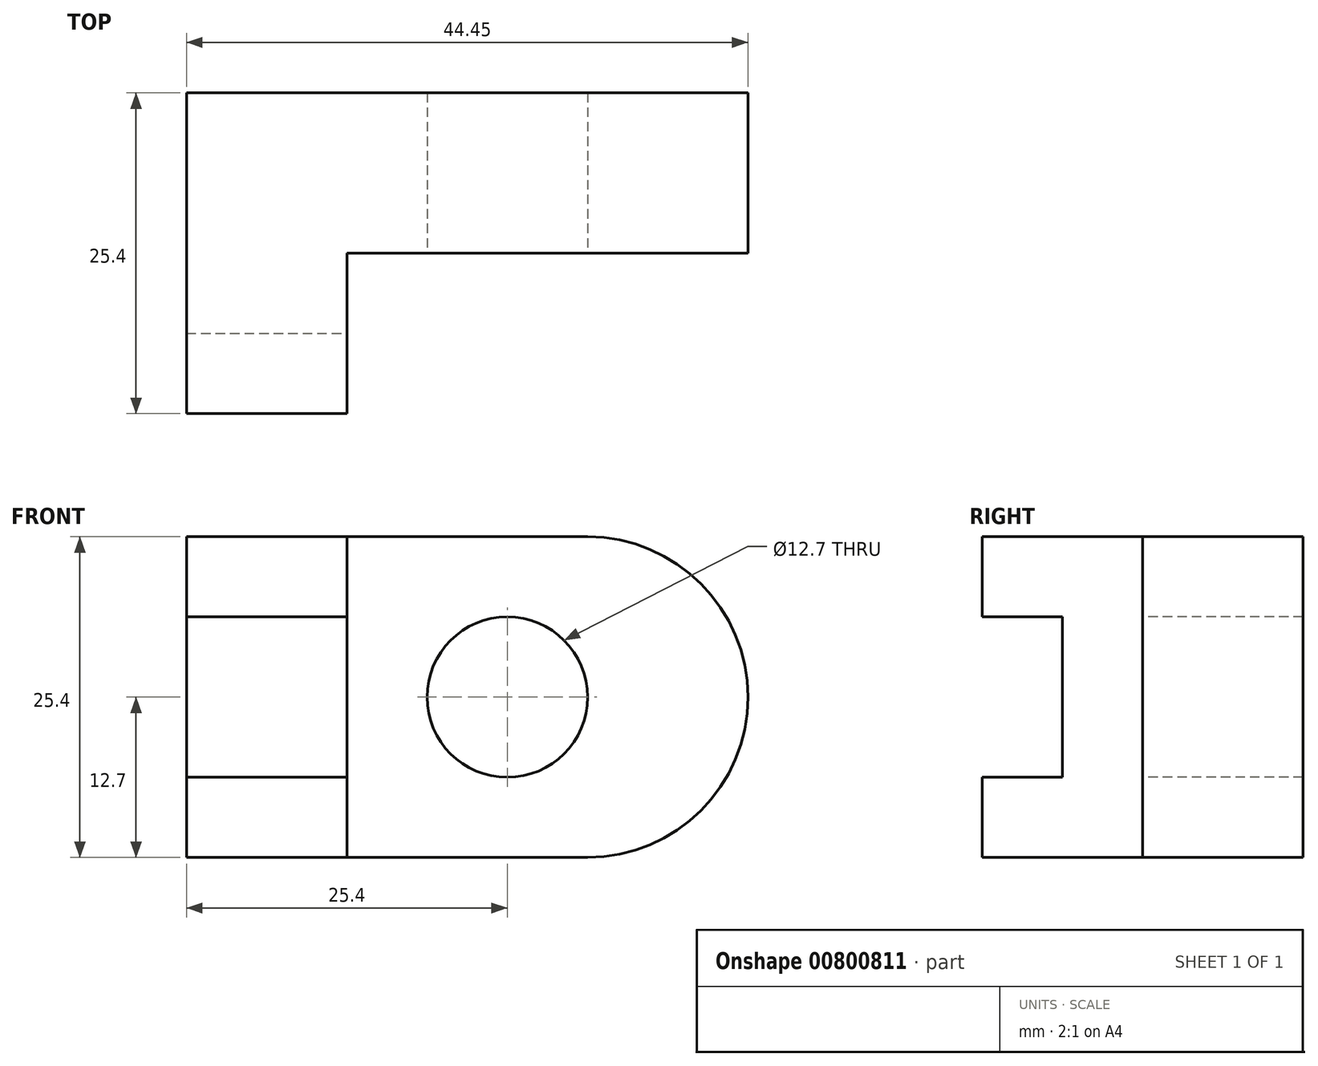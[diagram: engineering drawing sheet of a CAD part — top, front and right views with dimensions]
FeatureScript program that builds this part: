
annotation { "Feature Type Name" : "Feature", "Feature Type Description" : "" }
export const myFeature = defineFeature(function(context is Context, id is Id, definition is map)
    precondition{}
    {
        {
            var Q0;
            Q0=qCreatedBy(makeId("Top.planeOp"),FACE);
            var sketch = newSketch(context, id + "F0", { "sketchPlane" : qUnion([Q0])});
            skLineSegment(sketch, "E0", {"start": v(0, 0) * mm, "end": v(0, -12.7) * mm});
            skLineSegment(sketch, "E1", {"start": v(0, -12.7) * mm, "end": v(-12.7, -12.7) * mm});
            skLineSegment(sketch, "E2", {"start": v(-12.7, -12.7) * mm, "end": v(-12.7, 12.7) * mm});
            skLineSegment(sketch, "E3", {"start": v(-12.7, 12.7) * mm, "end": v(31.75, 12.7) * mm});
            skLineSegment(sketch, "E4", {"start": v(31.75, 12.7) * mm, "end": v(31.75, 0) * mm});
            skLineSegment(sketch, "E5", {"start": v(31.75, 0) * mm, "end": v(0, 0) * mm});
            skSolve(sketch);
        }
        {
            var Q0;
            Q0=makeQuery(id+"F0.imprint","IMPRINT",FACE,{"disambiguationData":[TD([[makeQuery(id+"F0.imprint","IMPRINT",EDGE,{"derivedFrom":sQuery(id+"F0.wireOp",EDGE,"E0")}),-1.0]])]});
            extrude(context, id + "F1", {"entities" : qUnion([Q0]), "depth" : 25.4 * mm, "offsetDistance" : 25.4 * mm});
        }
        {
            var Q0;
            Q0=makeQuery(id+"F1.opExtrude","SWEPT_FACE",FACE,{"disambiguationData":[OSD([sQuery(id+"F0.wireOp",EDGE,"E1")])]});
            var sketch = newSketch(context, id + "F2", { "sketchPlane" : qUnion([Q0])});
            skLineSegment(sketch, "E6", {"start": v(-12.7, 0) * mm, "end": v(-12.7, 6.35) * mm});
            skLineSegment(sketch, "E7", {"start": v(-12.7, 6.35) * mm, "end": v(0, 6.35) * mm});
            skLineSegment(sketch, "E8", {"start": v(0, 6.35) * mm, "end": v(0, 19.05) * mm});
            skLineSegment(sketch, "E9", {"start": v(0, 19.05) * mm, "end": v(-12.7, 19.05) * mm});
            skLineSegment(sketch, "E10", {"start": v(-12.7, 19.05) * mm, "end": v(-12.7, 6.35) * mm});
            skSolve(sketch);
        }
        {
            var Q0;
            Q0=makeQuery(id+"F2.imprint","IMPRINT",FACE,{"disambiguationData":[TD([[makeQuery(id+"F2.imprint","IMPRINT",EDGE,{"derivedFrom":sQuery(id+"F2.wireOp",EDGE,"E7")}),1.0]])]});
            extrude(context, id + "F3", {"entities" : qUnion([Q0]), "operationType" : NewBodyOperationType.REMOVE, "oppositeDirection" : true, "depth" : 6.35 * mm, "offsetDistance" : 25.4 * mm});
        }
        {
            var Q0;
            Q0=makeQuery(id+"F1.opExtrude","SWEPT_FACE",FACE,{"disambiguationData":[OSD([sQuery(id+"F0.wireOp",EDGE,"E5")])]});
            var sketch = newSketch(context, id + "F4", { "sketchPlane" : qUnion([Q0])});
            skLineSegment(sketch, "E11", {"start": v(0, 25.4) * mm, "end": v(12.7, 25.4) * mm, "construction": true});
            skLineSegment(sketch, "E12", {"start": v(0, 0) * mm, "end": v(12.7, 0) * mm, "construction": true});
            skLineSegment(sketch, "E13", {"start": v(12.7, 0) * mm, "end": v(19.05, 0) * mm, "construction": true});
            skLineSegment(sketch, "E14", {"start": v(12.7, 25.4) * mm, "end": v(19.05, 25.4) * mm, "construction": true});
            skArc(sketch, "E15", {"start": v(19.05, 0) * mm, "mid": v(31.75, 12.7) * mm, "end": v(19.05, 25.4) * mm});
            skLineSegment(sketch, "E16", {"start": v(19.05, 25.4) * mm, "end": v(0, 25.4) * mm});
            skLineSegment(sketch, "E17", {"start": v(19.05, 25.4) * mm, "end": v(31.75, 25.4) * mm});
            skLineSegment(sketch, "E18", {"start": v(31.75, 25.4) * mm, "end": v(31.75, 12.7) * mm});
            skLineSegment(sketch, "E19", {"start": v(19.05, 0) * mm, "end": v(31.75, 0) * mm});
            skLineSegment(sketch, "E20", {"start": v(31.75, 0) * mm, "end": v(31.75, 12.7) * mm});
            skSolve(sketch);
        }
        {
            var Q0;
            {var subQ0=sQuery(id+"F4.wireOp",EDGE,"E17");Q0=makeQuery(id+"F4.imprint","IMPRINT",FACE,{"disambiguationData":[TD([[makeQuery(id+"F4.imprint","IMPRINT",EDGE,{"derivedFrom":subQ0}),1.0]])]});}
            var Q1;
            {var subQ0=sQuery(id+"F4.wireOp",EDGE,"E19");Q1=makeQuery(id+"F4.imprint","IMPRINT",FACE,{"disambiguationData":[TD([[makeQuery(id+"F4.imprint","IMPRINT",EDGE,{"derivedFrom":subQ0}),-1.0]])]});}
            extrude(context, id + "F5", {"entities" : qUnion([Q0, Q1]), "operationType" : NewBodyOperationType.REMOVE, "oppositeDirection" : true, "depth" : 25.4 * mm, "offsetDistance" : 25.4 * mm});
        }
        {
            var Q0;
            Q0=makeQuery(id+"F1.opExtrude","SWEPT_FACE",FACE,{"disambiguationData":[OSD([sQuery(id+"F0.wireOp",EDGE,"E5")])]});
            var sketch = newSketch(context, id + "F6", { "sketchPlane" : qUnion([Q0])});
            skLineSegment(sketch, "E21", {"start": v(0, 25.4) * mm, "end": v(0, 21.7) * mm, "construction": true});
            skLineSegment(sketch, "E22", {"start": v(0, 25.4) * mm, "end": v(0, 12.7) * mm, "construction": true});
            skLineSegment(sketch, "E23", {"start": v(0, 12.7) * mm, "end": v(12.7, 12.7) * mm, "construction": true});
            skCircle(sketch, "E24", {"center": v(12.7, 12.7) * mm, "radius": 6.35 * mm});
            skSolve(sketch);
        }
        {
            var Q0;
            Q0=makeQuery(id+"F6.imprint","IMPRINT",FACE,{"disambiguationData":[TD([[makeQuery(id+"F6.imprint","IMPRINT",EDGE,{"derivedFrom":sQuery(id+"F6.wireOp",EDGE,"E24")}),1.0]])]});
            extrude(context, id + "F7", {"entities" : qUnion([Q0]), "operationType" : NewBodyOperationType.REMOVE, "oppositeDirection" : true, "depth" : 25.4 * mm, "offsetDistance" : 25.4 * mm});
        }
    });
